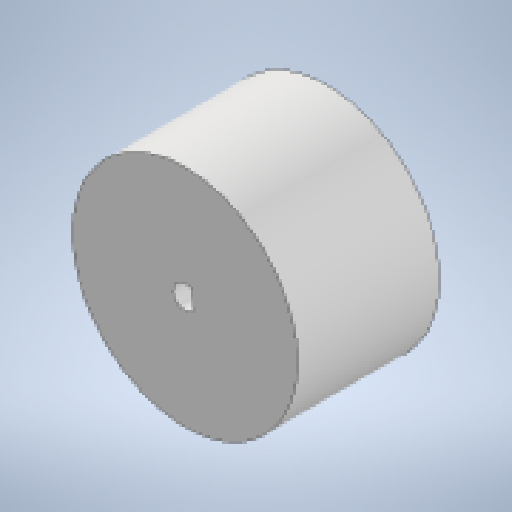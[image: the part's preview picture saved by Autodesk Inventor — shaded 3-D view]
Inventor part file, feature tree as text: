
AUTODESK INVENTOR PART (.ipt)
format: ipt  version: 2023 (Build 270158000, 158)  size: 132,608 bytes
history: native  units: in
note: dims shown in document units (in); Inventor stores cm internally (conversion verified against a paired STEP export)
features: other x5, reference x2, sketch x1, extrude x1
ambient origin geometry x8: Origin, YZ Plane, XZ Plane, XY Plane, X Axis, Y Axis, Z Axis, Center Point
bodies: Body1 (feature_tree)
feature tree (9):
  other  "Bryła1"
  sketch  "Szkic1"
  other  "Płaszczyzna konstrukcyjna1"
  extrude  "Wyciągnięcie proste1"  Depth=1.1417in
  reference  "Odniesienie1"
  reference  "Odniesienie2"
  other  "<userpath>\Desktop\MojeRoboty\Stefan\mechanics\STEFAN_2.0.iam"
  other  "STEFAN_2.0.iam"
  other  "n20 motor:2"
